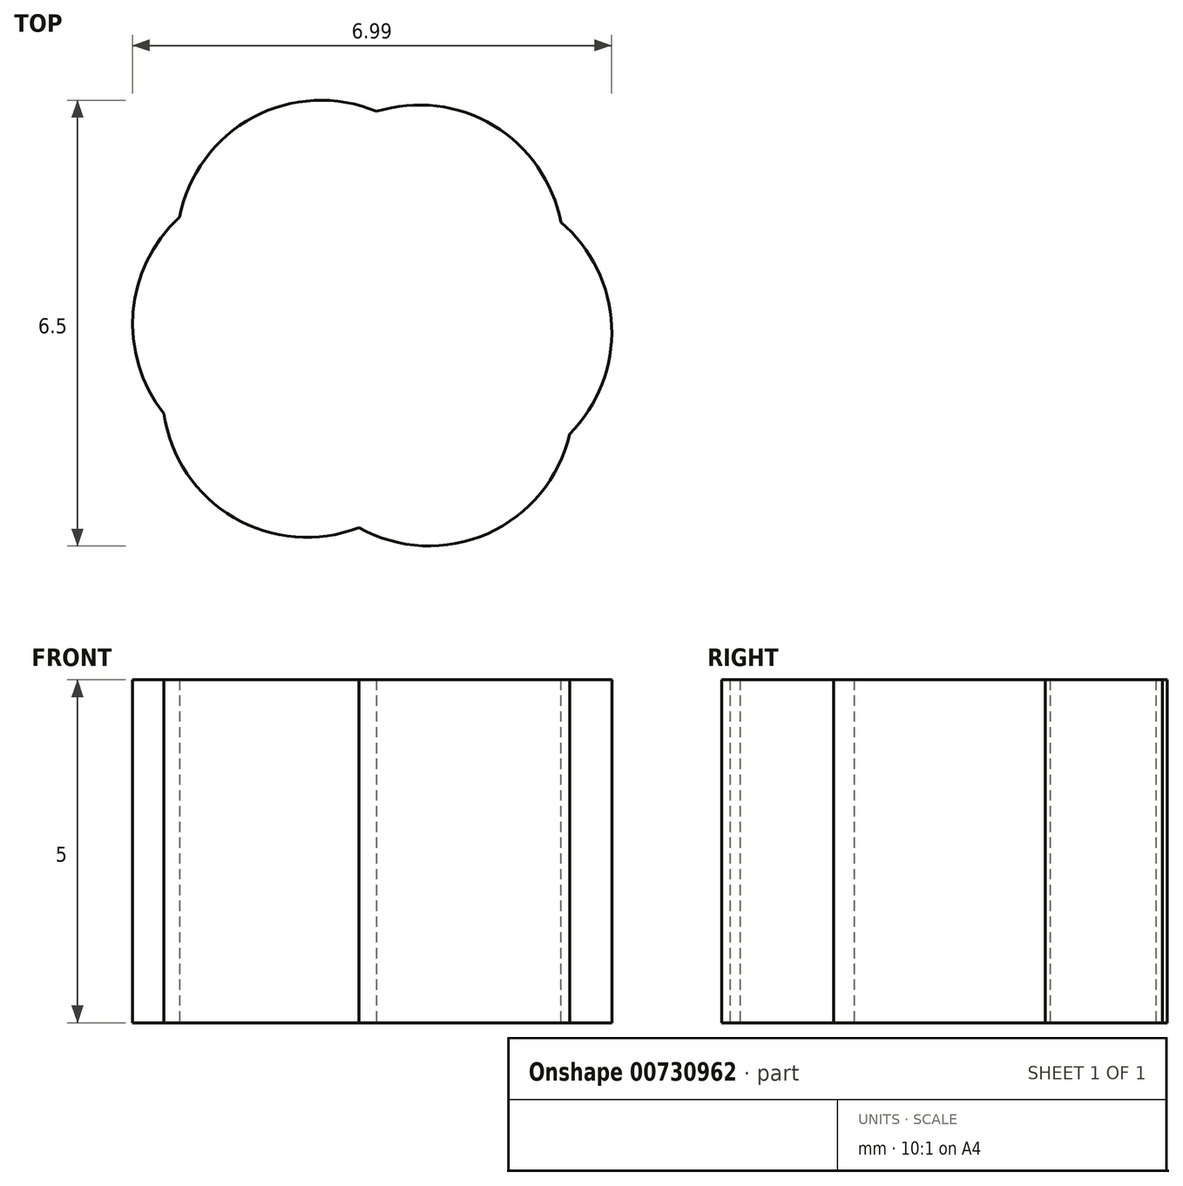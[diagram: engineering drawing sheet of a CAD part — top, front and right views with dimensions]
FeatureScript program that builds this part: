
annotation { "Feature Type Name" : "Feature", "Feature Type Description" : "" }
export const myFeature = defineFeature(function(context is Context, id is Id, definition is map)
    precondition{}
    {
        {
            var Q0;
            Q0=qCreatedBy(makeId("Top.planeOp"),FACE);
            var sketch = newSketch(context, id + "F0", { "sketchPlane" : qUnion([Q0])});
            skCircle(sketch, "E0", {"center": v(-28.39, 11.68) * mm, "radius": 2.1 * mm});
            skCircle(sketch, "E1", {"center": v(-27.95, 10.67) * mm, "radius": 2.1 * mm});
            skCircle(sketch, "E2", {"center": v(-25.6, 11.56) * mm, "radius": 2.1 * mm});
            skCircle(sketch, "E3", {"center": v(-26.3, 12.77) * mm, "radius": 2.1 * mm});
            skCircle(sketch, "E4", {"center": v(-26.16, 10.54) * mm, "radius": 2.1 * mm});
            skCircle(sketch, "E5", {"center": v(-27.74, 12.84) * mm, "radius": 2.1 * mm});
            skCircle(sketch, "E6", {"center": v(-27, 11.63) * mm, "radius": 3.5 * mm});
            skSolve(sketch);
        }
        {
            var Q0;
            {var subQ0=sQuery(id+"F0.wireOp",EDGE,"E6");var subQ1=sQuery(id+"F0.wireOp",EDGE,"E2");var subQ2=makeQuery(id+"F0.imprint","INTERSECT",VERTEX,{"disambiguationData":[OD(0.0)],"derivedFrom":[subQ1,subQ0]});Q0=makeQuery(id+"F0.imprint","IMPRINT",FACE,{"disambiguationData":[TD([[makeQuery(id+"F0.imprint","IMPRINT",EDGE,{"disambiguationData":[TD([[subQ2,1.0]])],"derivedFrom":subQ1}),1.0]])]});}
            var Q1;
            {var subQ0=sQuery(id+"F0.wireOp",EDGE,"E6");var subQ1=sQuery(id+"F0.wireOp",EDGE,"E5");var subQ2=makeQuery(id+"F0.imprint","INTERSECT",VERTEX,{"disambiguationData":[OD(0.0)],"derivedFrom":[subQ1,subQ0]});Q1=makeQuery(id+"F0.imprint","IMPRINT",FACE,{"disambiguationData":[TD([[makeQuery(id+"F0.imprint","IMPRINT",EDGE,{"disambiguationData":[TD([[subQ2,-1.0]])],"derivedFrom":subQ1}),1.0]])]});}
            var Q2;
            {var subQ3=sQuery(id+"F0.wireOp",EDGE,"E0");var subQ5=sQuery(id+"F0.wireOp",EDGE,"E3");var subQ6=makeQuery(id+"F0.imprint","INTERSECT",VERTEX,{"disambiguationData":[OD(0.0)],"derivedFrom":[subQ3,subQ5]});Q2=makeQuery(id+"F0.imprint","IMPRINT",FACE,{"disambiguationData":[TD([[makeQuery(id+"F0.imprint","IMPRINT",EDGE,{"disambiguationData":[TD([[subQ6,-1.0]])],"derivedFrom":subQ3}),-1.0]])]});}
            var Q3;
            {var subQ1=sQuery(id+"F0.wireOp",EDGE,"E2");var subQ6=sQuery(id+"F0.wireOp",EDGE,"E6");var subQ8=makeQuery(id+"F0.imprint","INTERSECT",VERTEX,{"disambiguationData":[OD(0.0)],"derivedFrom":[subQ1,subQ6]});Q3=makeQuery(id+"F0.imprint","IMPRINT",FACE,{"disambiguationData":[TD([[makeQuery(id+"F0.imprint","IMPRINT",EDGE,{"disambiguationData":[TD([[subQ8,-1.0]])],"derivedFrom":subQ1}),1.0]])]});}
            var Q4;
            {var subQ0=sQuery(id+"F0.wireOp",EDGE,"E3");var subQ1=sQuery(id+"F0.wireOp",EDGE,"E0");var subQ2=makeQuery(id+"F0.imprint","INTERSECT",VERTEX,{"disambiguationData":[OD(0.0)],"derivedFrom":[subQ1,subQ0]});Q4=makeQuery(id+"F0.imprint","IMPRINT",FACE,{"disambiguationData":[TD([[makeQuery(id+"F0.imprint","IMPRINT",EDGE,{"disambiguationData":[TD([[subQ2,-1.0]])],"derivedFrom":subQ1}),1.0]])]});}
            var Q5;
            {var subQ0=sQuery(id+"F0.wireOp",EDGE,"E2");var subQ1=sQuery(id+"F0.wireOp",EDGE,"E0");var subQ2=makeQuery(id+"F0.imprint","INTERSECT",VERTEX,{"disambiguationData":[OD(0.0)],"derivedFrom":[subQ1,subQ0]});Q5=makeQuery(id+"F0.imprint","IMPRINT",FACE,{"disambiguationData":[TD([[makeQuery(id+"F0.imprint","IMPRINT",EDGE,{"disambiguationData":[TD([[subQ2,-1.0]])],"derivedFrom":subQ1}),-1.0]])]});}
            var Q6;
            {var subQ0=sQuery(id+"F0.wireOp",EDGE,"E3");var subQ1=sQuery(id+"F0.wireOp",EDGE,"E2");var subQ2=makeQuery(id+"F0.imprint","INTERSECT",VERTEX,{"disambiguationData":[OD(0.0)],"derivedFrom":[subQ1,subQ0]});Q6=makeQuery(id+"F0.imprint","IMPRINT",FACE,{"disambiguationData":[TD([[makeQuery(id+"F0.imprint","IMPRINT",EDGE,{"disambiguationData":[TD([[subQ2,-1.0]])],"derivedFrom":subQ1}),-1.0]])]});}
            var Q7;
            {var subQ0=sQuery(id+"F0.wireOp",EDGE,"E4");var subQ1=sQuery(id+"F0.wireOp",EDGE,"E1");var subQ2=makeQuery(id+"F0.imprint","INTERSECT",VERTEX,{"disambiguationData":[OD(1.0)],"derivedFrom":[subQ1,subQ0]});Q7=makeQuery(id+"F0.imprint","IMPRINT",FACE,{"disambiguationData":[TD([[makeQuery(id+"F0.imprint","IMPRINT",EDGE,{"disambiguationData":[TD([[subQ2,-1.0]])],"derivedFrom":subQ1}),-1.0]])]});}
            var Q8;
            {var subQ0=sQuery(id+"F0.wireOp",EDGE,"E1");var subQ1=sQuery(id+"F0.wireOp",EDGE,"E0");var subQ2=makeQuery(id+"F0.imprint","INTERSECT",VERTEX,{"disambiguationData":[OD(1.0)],"derivedFrom":[subQ1,subQ0]});Q8=makeQuery(id+"F0.imprint","IMPRINT",FACE,{"disambiguationData":[TD([[makeQuery(id+"F0.imprint","IMPRINT",EDGE,{"disambiguationData":[TD([[subQ2,-1.0]])],"derivedFrom":subQ1}),-1.0]])]});}
            var Q9;
            {var subQ0=sQuery(id+"F0.wireOp",EDGE,"E5");var subQ1=sQuery(id+"F0.wireOp",EDGE,"E0");var subQ2=makeQuery(id+"F0.imprint","INTERSECT",VERTEX,{"disambiguationData":[OD(0.0)],"derivedFrom":[subQ1,subQ0]});Q9=makeQuery(id+"F0.imprint","IMPRINT",FACE,{"disambiguationData":[TD([[makeQuery(id+"F0.imprint","IMPRINT",EDGE,{"disambiguationData":[TD([[subQ2,-1.0]])],"derivedFrom":subQ1}),1.0]])]});}
            var Q10;
            {var subQ0=sQuery(id+"F0.wireOp",EDGE,"E4");var subQ1=sQuery(id+"F0.wireOp",EDGE,"E0");var subQ2=makeQuery(id+"F0.imprint","INTERSECT",VERTEX,{"disambiguationData":[OD(1.0)],"derivedFrom":[subQ1,subQ0]});Q10=makeQuery(id+"F0.imprint","IMPRINT",FACE,{"disambiguationData":[TD([[makeQuery(id+"F0.imprint","IMPRINT",EDGE,{"disambiguationData":[TD([[subQ2,-1.0]])],"derivedFrom":subQ1}),-1.0]])]});}
            var Q11;
            {var subQ0=sQuery(id+"F0.wireOp",EDGE,"E3");var subQ1=sQuery(id+"F0.wireOp",EDGE,"E1");var subQ2=makeQuery(id+"F0.imprint","INTERSECT",VERTEX,{"disambiguationData":[OD(0.0)],"derivedFrom":[subQ1,subQ0]});Q11=makeQuery(id+"F0.imprint","IMPRINT",FACE,{"disambiguationData":[TD([[makeQuery(id+"F0.imprint","IMPRINT",EDGE,{"disambiguationData":[TD([[subQ2,1.0]])],"derivedFrom":subQ1}),-1.0]])]});}
            var Q12;
            {var subQ0=sQuery(id+"F0.wireOp",EDGE,"E3");var subQ1=sQuery(id+"F0.wireOp",EDGE,"E2");var subQ2=makeQuery(id+"F0.imprint","INTERSECT",VERTEX,{"disambiguationData":[OD(0.0)],"derivedFrom":[subQ1,subQ0]});Q12=makeQuery(id+"F0.imprint","IMPRINT",FACE,{"disambiguationData":[TD([[makeQuery(id+"F0.imprint","IMPRINT",EDGE,{"disambiguationData":[TD([[subQ2,-1.0]])],"derivedFrom":subQ1}),1.0]])]});}
            var Q13;
            {var subQ0=sQuery(id+"F0.wireOp",EDGE,"E5");var subQ1=sQuery(id+"F0.wireOp",EDGE,"E1");var subQ2=makeQuery(id+"F0.imprint","INTERSECT",VERTEX,{"disambiguationData":[OD(0.0)],"derivedFrom":[subQ1,subQ0]});Q13=makeQuery(id+"F0.imprint","IMPRINT",FACE,{"disambiguationData":[TD([[makeQuery(id+"F0.imprint","IMPRINT",EDGE,{"disambiguationData":[TD([[subQ2,1.0]])],"derivedFrom":subQ1}),-1.0]])]});}
            var Q14;
            {var subQ0=sQuery(id+"F0.wireOp",EDGE,"E1");var subQ1=sQuery(id+"F0.wireOp",EDGE,"E0");var subQ2=makeQuery(id+"F0.imprint","INTERSECT",VERTEX,{"disambiguationData":[OD(1.0)],"derivedFrom":[subQ1,subQ0]});Q14=makeQuery(id+"F0.imprint","IMPRINT",FACE,{"disambiguationData":[TD([[makeQuery(id+"F0.imprint","IMPRINT",EDGE,{"disambiguationData":[TD([[subQ2,-1.0]])],"derivedFrom":subQ1}),1.0]])]});}
            var Q15;
            {var subQ0=sQuery(id+"F0.wireOp",EDGE,"E3");var subQ1=sQuery(id+"F0.wireOp",EDGE,"E1");var subQ2=makeQuery(id+"F0.imprint","INTERSECT",VERTEX,{"disambiguationData":[OD(1.0)],"derivedFrom":[subQ1,subQ0]});Q15=makeQuery(id+"F0.imprint","IMPRINT",FACE,{"disambiguationData":[TD([[makeQuery(id+"F0.imprint","IMPRINT",EDGE,{"disambiguationData":[TD([[subQ2,-1.0]])],"derivedFrom":subQ1}),1.0]])]});}
            var Q16;
            {var subQ0=sQuery(id+"F0.wireOp",EDGE,"E2");var subQ1=sQuery(id+"F0.wireOp",EDGE,"E1");var subQ2=makeQuery(id+"F0.imprint","INTERSECT",VERTEX,{"disambiguationData":[OD(0.0)],"derivedFrom":[subQ1,subQ0]});Q16=makeQuery(id+"F0.imprint","IMPRINT",FACE,{"disambiguationData":[TD([[makeQuery(id+"F0.imprint","IMPRINT",EDGE,{"disambiguationData":[TD([[subQ2,-1.0]])],"derivedFrom":subQ1}),1.0]])]});}
            var Q17;
            {var subQ0=sQuery(id+"F0.wireOp",EDGE,"E4");var subQ1=sQuery(id+"F0.wireOp",EDGE,"E0");var subQ2=makeQuery(id+"F0.imprint","INTERSECT",VERTEX,{"disambiguationData":[OD(0.0)],"derivedFrom":[subQ1,subQ0]});Q17=makeQuery(id+"F0.imprint","IMPRINT",FACE,{"disambiguationData":[TD([[makeQuery(id+"F0.imprint","IMPRINT",EDGE,{"disambiguationData":[TD([[subQ2,-1.0]])],"derivedFrom":subQ1}),-1.0]])]});}
            var Q18;
            {var subQ0=sQuery(id+"F0.wireOp",EDGE,"E4");var subQ1=sQuery(id+"F0.wireOp",EDGE,"E0");var subQ2=makeQuery(id+"F0.imprint","INTERSECT",VERTEX,{"disambiguationData":[OD(1.0)],"derivedFrom":[subQ1,subQ0]});Q18=makeQuery(id+"F0.imprint","IMPRINT",FACE,{"disambiguationData":[TD([[makeQuery(id+"F0.imprint","IMPRINT",EDGE,{"disambiguationData":[TD([[subQ2,-1.0]])],"derivedFrom":subQ1}),1.0]])]});}
            var Q19;
            {var subQ0=sQuery(id+"F0.wireOp",EDGE,"E2");var subQ1=sQuery(id+"F0.wireOp",EDGE,"E0");var subQ2=makeQuery(id+"F0.imprint","INTERSECT",VERTEX,{"disambiguationData":[OD(0.0)],"derivedFrom":[subQ1,subQ0]});Q19=makeQuery(id+"F0.imprint","IMPRINT",FACE,{"disambiguationData":[TD([[makeQuery(id+"F0.imprint","IMPRINT",EDGE,{"disambiguationData":[TD([[subQ2,-1.0]])],"derivedFrom":subQ1}),1.0]])]});}
            var Q20;
            {var subQ0=sQuery(id+"F0.wireOp",EDGE,"E2");var subQ1=sQuery(id+"F0.wireOp",EDGE,"E0");var subQ2=makeQuery(id+"F0.imprint","INTERSECT",VERTEX,{"disambiguationData":[OD(1.0)],"derivedFrom":[subQ1,subQ0]});Q20=makeQuery(id+"F0.imprint","IMPRINT",FACE,{"disambiguationData":[TD([[makeQuery(id+"F0.imprint","IMPRINT",EDGE,{"disambiguationData":[TD([[subQ2,-1.0]])],"derivedFrom":subQ1}),-1.0]])]});}
            var Q21;
            {var subQ0=sQuery(id+"F0.wireOp",EDGE,"E3");var subQ1=sQuery(id+"F0.wireOp",EDGE,"E0");var subQ2=makeQuery(id+"F0.imprint","INTERSECT",VERTEX,{"disambiguationData":[OD(1.0)],"derivedFrom":[subQ1,subQ0]});Q21=makeQuery(id+"F0.imprint","IMPRINT",FACE,{"disambiguationData":[TD([[makeQuery(id+"F0.imprint","IMPRINT",EDGE,{"disambiguationData":[TD([[subQ2,-1.0]])],"derivedFrom":subQ1}),-1.0]])]});}
            var Q22;
            {var subQ0=sQuery(id+"F0.wireOp",EDGE,"E2");var subQ1=sQuery(id+"F0.wireOp",EDGE,"E0");var subQ2=makeQuery(id+"F0.imprint","INTERSECT",VERTEX,{"disambiguationData":[OD(1.0)],"derivedFrom":[subQ1,subQ0]});Q22=makeQuery(id+"F0.imprint","IMPRINT",FACE,{"disambiguationData":[TD([[makeQuery(id+"F0.imprint","IMPRINT",EDGE,{"disambiguationData":[TD([[subQ2,-1.0]])],"derivedFrom":subQ1}),1.0]])]});}
            var Q23;
            {var subQ0=sQuery(id+"F0.wireOp",EDGE,"E3");var subQ1=sQuery(id+"F0.wireOp",EDGE,"E2");var subQ2=makeQuery(id+"F0.imprint","INTERSECT",VERTEX,{"disambiguationData":[OD(1.0)],"derivedFrom":[subQ1,subQ0]});Q23=makeQuery(id+"F0.imprint","IMPRINT",FACE,{"disambiguationData":[TD([[makeQuery(id+"F0.imprint","IMPRINT",EDGE,{"disambiguationData":[TD([[subQ2,-1.0]])],"derivedFrom":subQ1}),-1.0]])]});}
            var Q24;
            {var subQ0=sQuery(id+"F0.wireOp",EDGE,"E3");var subQ1=sQuery(id+"F0.wireOp",EDGE,"E2");var subQ2=makeQuery(id+"F0.imprint","INTERSECT",VERTEX,{"disambiguationData":[OD(1.0)],"derivedFrom":[subQ1,subQ0]});Q24=makeQuery(id+"F0.imprint","IMPRINT",FACE,{"disambiguationData":[TD([[makeQuery(id+"F0.imprint","IMPRINT",EDGE,{"disambiguationData":[TD([[subQ2,-1.0]])],"derivedFrom":subQ1}),1.0]])]});}
            var Q25;
            {var subQ0=sQuery(id+"F0.wireOp",EDGE,"E3");var subQ1=sQuery(id+"F0.wireOp",EDGE,"E0");var subQ2=makeQuery(id+"F0.imprint","INTERSECT",VERTEX,{"disambiguationData":[OD(1.0)],"derivedFrom":[subQ1,subQ0]});Q25=makeQuery(id+"F0.imprint","IMPRINT",FACE,{"disambiguationData":[TD([[makeQuery(id+"F0.imprint","IMPRINT",EDGE,{"disambiguationData":[TD([[subQ2,-1.0]])],"derivedFrom":subQ1}),1.0]])]});}
            var Q26;
            {var subQ0=sQuery(id+"F0.wireOp",EDGE,"E1");var subQ1=sQuery(id+"F0.wireOp",EDGE,"E0");var subQ2=makeQuery(id+"F0.imprint","INTERSECT",VERTEX,{"disambiguationData":[OD(0.0)],"derivedFrom":[subQ1,subQ0]});Q26=makeQuery(id+"F0.imprint","IMPRINT",FACE,{"disambiguationData":[TD([[makeQuery(id+"F0.imprint","IMPRINT",EDGE,{"disambiguationData":[TD([[subQ2,1.0]])],"derivedFrom":subQ1}),-1.0]])]});}
            var Q27;
            {var subQ0=sQuery(id+"F0.wireOp",EDGE,"E4");var subQ1=sQuery(id+"F0.wireOp",EDGE,"E0");var subQ2=makeQuery(id+"F0.imprint","INTERSECT",VERTEX,{"disambiguationData":[OD(0.0)],"derivedFrom":[subQ1,subQ0]});Q27=makeQuery(id+"F0.imprint","IMPRINT",FACE,{"disambiguationData":[TD([[makeQuery(id+"F0.imprint","IMPRINT",EDGE,{"disambiguationData":[TD([[subQ2,1.0]])],"derivedFrom":subQ1}),-1.0]])]});}
            var Q28;
            {var subQ0=sQuery(id+"F0.wireOp",EDGE,"E4");var subQ1=sQuery(id+"F0.wireOp",EDGE,"E0");var subQ2=makeQuery(id+"F0.imprint","INTERSECT",VERTEX,{"disambiguationData":[OD(0.0)],"derivedFrom":[subQ1,subQ0]});Q28=makeQuery(id+"F0.imprint","IMPRINT",FACE,{"disambiguationData":[TD([[makeQuery(id+"F0.imprint","IMPRINT",EDGE,{"disambiguationData":[TD([[subQ2,1.0]])],"derivedFrom":subQ1}),1.0]])]});}
            var Q29;
            {var subQ0=sQuery(id+"F0.wireOp",EDGE,"E4");var subQ1=sQuery(id+"F0.wireOp",EDGE,"E0");var subQ2=makeQuery(id+"F0.imprint","INTERSECT",VERTEX,{"disambiguationData":[OD(0.0)],"derivedFrom":[subQ1,subQ0]});Q29=makeQuery(id+"F0.imprint","IMPRINT",FACE,{"disambiguationData":[TD([[makeQuery(id+"F0.imprint","IMPRINT",EDGE,{"disambiguationData":[TD([[subQ2,-1.0]])],"derivedFrom":subQ1}),1.0]])]});}
            var Q30;
            {var subQ0=sQuery(id+"F0.wireOp",EDGE,"E4");var subQ1=sQuery(id+"F0.wireOp",EDGE,"E1");var subQ2=makeQuery(id+"F0.imprint","INTERSECT",VERTEX,{"disambiguationData":[OD(0.0)],"derivedFrom":[subQ1,subQ0]});Q30=makeQuery(id+"F0.imprint","IMPRINT",FACE,{"disambiguationData":[TD([[makeQuery(id+"F0.imprint","IMPRINT",EDGE,{"disambiguationData":[TD([[subQ2,-1.0]])],"derivedFrom":subQ1}),1.0]])]});}
            var Q31;
            {var subQ0=sQuery(id+"F0.wireOp",EDGE,"E4");var subQ1=sQuery(id+"F0.wireOp",EDGE,"E2");var subQ2=makeQuery(id+"F0.imprint","INTERSECT",VERTEX,{"disambiguationData":[OD(0.0)],"derivedFrom":[subQ1,subQ0]});Q31=makeQuery(id+"F0.imprint","IMPRINT",FACE,{"disambiguationData":[TD([[makeQuery(id+"F0.imprint","IMPRINT",EDGE,{"disambiguationData":[TD([[subQ2,-1.0]])],"derivedFrom":subQ1}),-1.0]])]});}
            var Q32;
            {var subQ7=sQuery(id+"F0.wireOp",EDGE,"E1");var subQ8=sQuery(id+"F0.wireOp",EDGE,"E0");var subQ9=makeQuery(id+"F0.imprint","INTERSECT",VERTEX,{"disambiguationData":[OD(0.0)],"derivedFrom":[subQ8,subQ7]});Q32=makeQuery(id+"F0.imprint","IMPRINT",FACE,{"disambiguationData":[TD([[makeQuery(id+"F0.imprint","IMPRINT",EDGE,{"disambiguationData":[TD([[subQ9,1.0]])],"derivedFrom":subQ8}),1.0]])]});}
            extrude(context, id + "F1", {"entities" : qUnion([Q0, Q1, Q2, Q3, Q4, Q5, Q6, Q7, Q8, Q9, Q10, Q11, Q12, Q13, Q14, Q15, Q16, Q17, Q18, Q19, Q20, Q21, Q22, Q23, Q24, Q25, Q26, Q27, Q28, Q29, Q30, Q31, Q32]), "depth" : 5 * mm, "offsetDistance" : 25.4 * mm});
        }
    });
